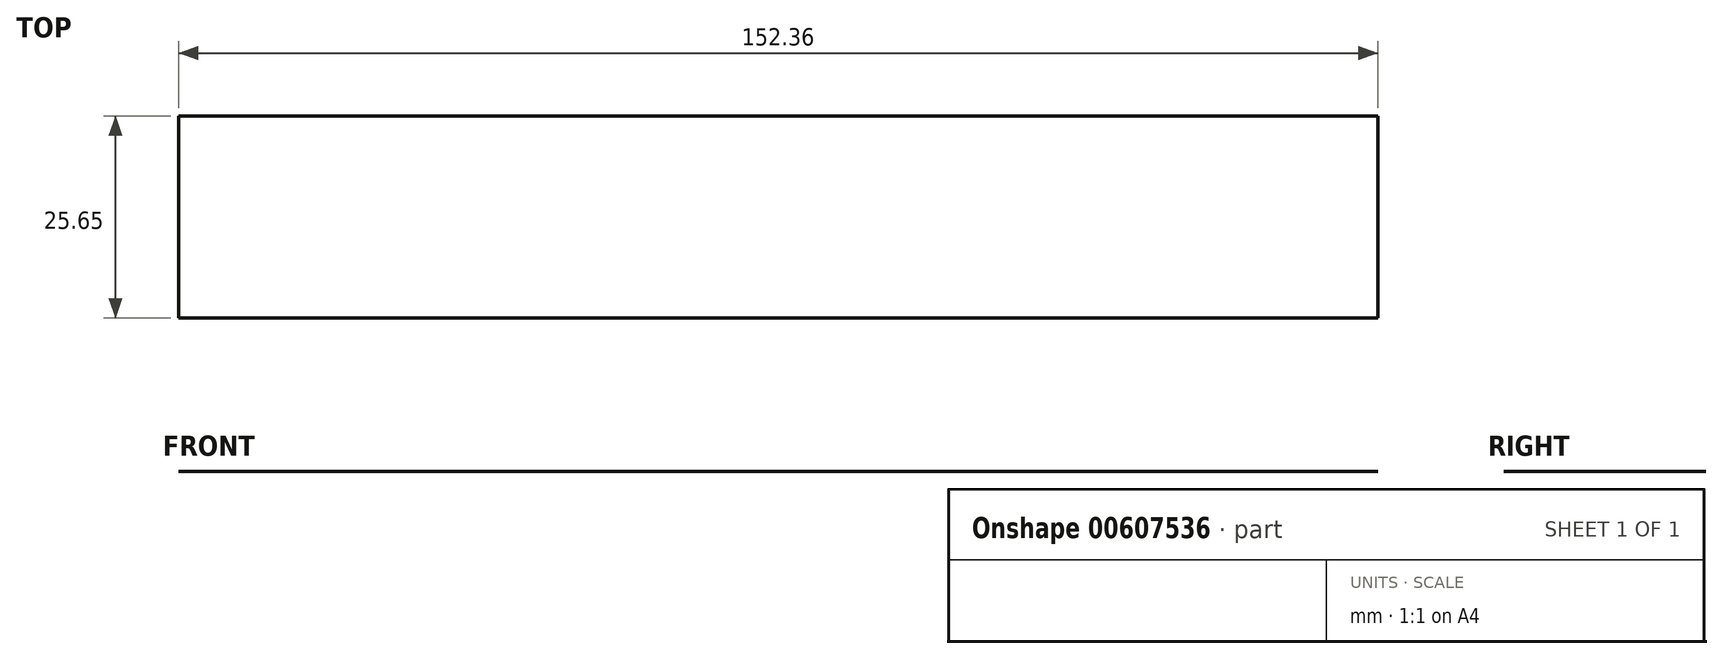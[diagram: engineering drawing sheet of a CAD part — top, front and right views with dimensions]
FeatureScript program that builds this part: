
annotation { "Feature Type Name" : "Feature", "Feature Type Description" : "" }
export const myFeature = defineFeature(function(context is Context, id is Id, definition is map)
    precondition{}
    {
        {
            var Q0;
            Q0=qCreatedBy(makeId("Front.planeOp"),FACE);
            var sketch = newSketch(context, id + "F0", { "sketchPlane" : qUnion([Q0])});
            skLineSegment(sketch, "E0.bottom", {"start": v(-76.18, -18.4) * mm, "end": v(76.18, -18.4) * mm});
            skLineSegment(sketch, "E0.top", {"start": v(-76.18, 18.4) * mm, "end": v(76.18, 18.4) * mm});
            skLineSegment(sketch, "E0.left", {"start": v(-76.18, -18.4) * mm, "end": v(-76.18, 18.4) * mm});
            skLineSegment(sketch, "E0.right", {"start": v(76.18, -18.4) * mm, "end": v(76.18, 18.4) * mm});
            skPoint(sketch, "E0.middle", {"position": v(0, 0) * mm});
            skSolve(sketch);
        }
        {
            var Q0;
            Q0=sQuery(id+"F0.wireOp",EDGE,"E0.top");
            extrude(context, id + "F1", {"bodyType" : ToolBodyType.SURFACE, "surfaceEntities" : qUnion([Q0]), "depth" : 25.65 * mm, "offsetDistance" : 25.4 * mm});
        }
    });
